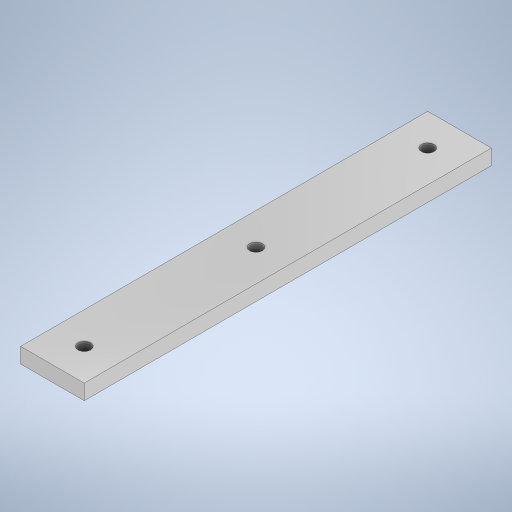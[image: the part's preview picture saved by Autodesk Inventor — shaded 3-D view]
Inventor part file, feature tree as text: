
AUTODESK INVENTOR PART (.ipt)
format: ipt  version: 2023 (Build 270158000, 158)  size: 264,704 bytes
history: native  units: mm
features: sketch x3, hole x2, thread x2, extrude x1
ambient origin geometry x8: Origin, YZ Plane, XZ Plane, XY Plane, X Axis, Y Axis, Z Axis, Center Point
bodies: Solid1 (feature_tree)
feature tree (8):
  extrude  "Extrusion1"  Depth=160.0mm
  hole  "Hole1"  [1 undecoded]
  hole  "Furo2"  [1 undecoded]
  thread  "Rosca1"  [1 undecoded]
  thread  "Rosca2"  [1 undecoded]
  sketch  "Sketch1"  dims[d0=25.0mm d1=160.0mm]
  sketch  "Sketch2"  dims[d2=6.0mm d3=0.0mm d4=25.0mm]
  sketch  "Esboço3"  dims[d5=160.0mm d6=12.5mm d7=12.5mm d8=12.5mm d9=12.5mm d10=5.0mm d11=6.0mm d12=4.0mm d13=2.0mm d14=90.0deg d15=0.5mm d16=20.594885mm d17=160.0mm d18=25.0mm d19=12.5mm d20=80.0mm d21=5.0mm d22=6.0mm d23=7.0mm d24=2.0mm d25=90.0deg d26=0.5mm d27=20.594885mm d28=43.6mm d29=0.0mm d30=15.0mm d31=0.0mm]
note: 4 required parameter values undecoded (feature->parameter linkage not recoverable at this tier; creation-order binding heuristic only, values carry confidence <= 0.55)
